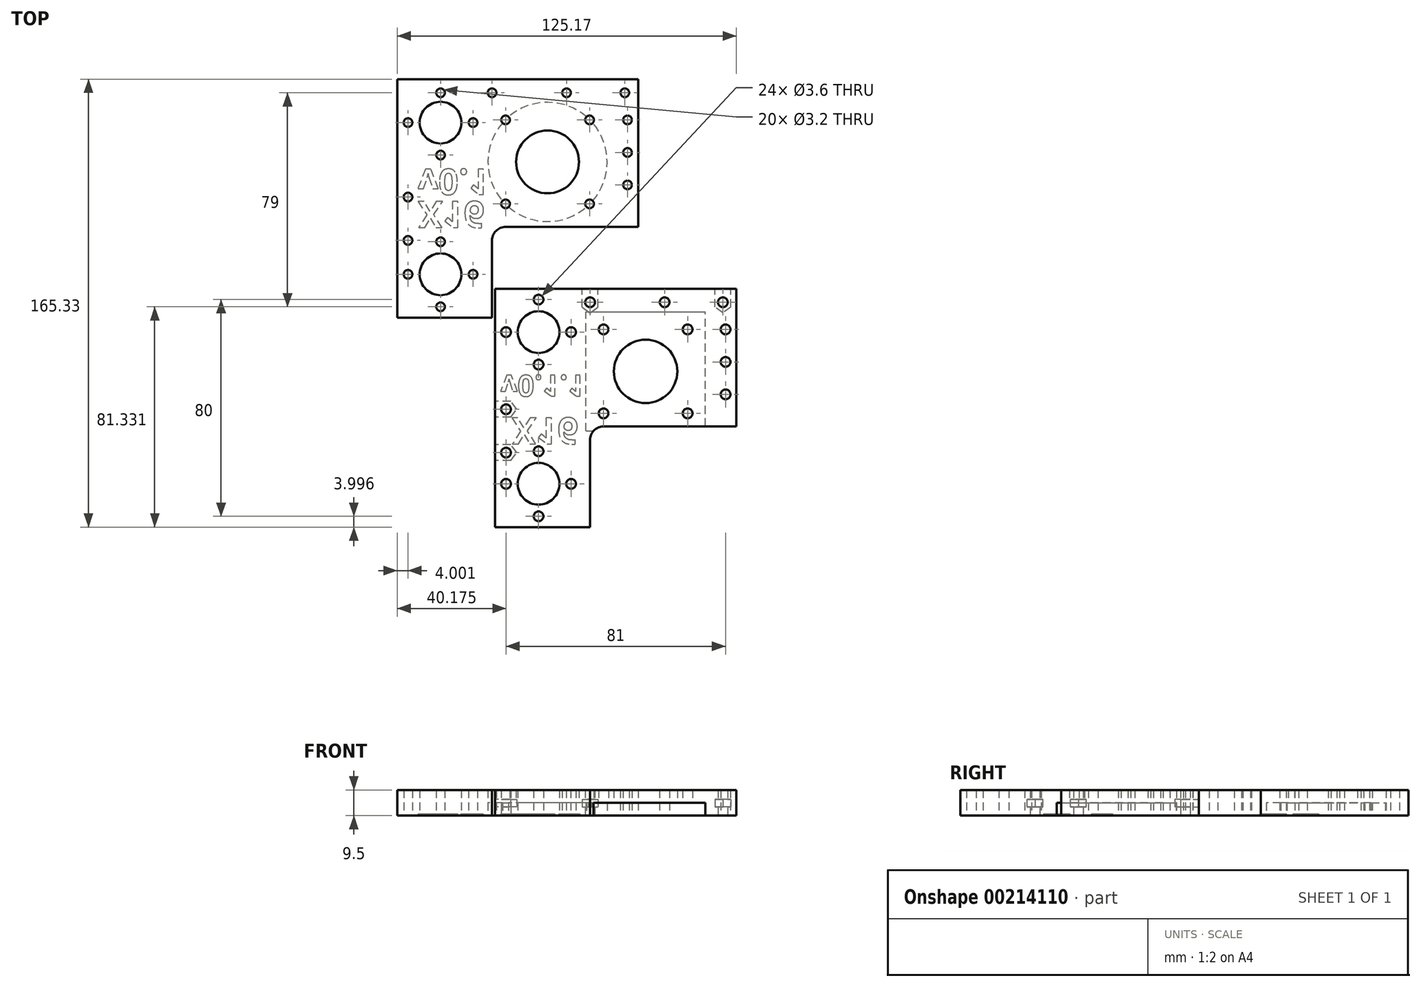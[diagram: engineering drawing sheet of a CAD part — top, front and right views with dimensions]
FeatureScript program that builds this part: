
annotation { "Feature Type Name" : "Feature", "Feature Type Description" : "" }
export const myFeature = defineFeature(function(context is Context, id is Id, definition is map)
    precondition{}
    {
        {
            var Q0;
            Q0=qCreatedBy(makeId("Top.planeOp"),FACE);
            var sketch = newSketch(context, id + "F0", { "sketchPlane" : qUnion([Q0])});
            skLineSegment(sketch, "E0", {"start": v(-66.99, 73.58) * mm, "end": v(-50.99, 73.58) * mm});
            skLineSegment(sketch, "E1", {"start": v(-50.99, 73.58) * mm, "end": v(-31.99, 73.58) * mm});
            skLineSegment(sketch, "E2", {"start": v(-31.99, 73.58) * mm, "end": v(-11.49, 73.58) * mm});
            skLineSegment(sketch, "E3", {"start": v(-11.49, 73.58) * mm, "end": v(-4.49, 73.58) * mm});
            skLineSegment(sketch, "E4", {"start": v(-4.49, 73.58) * mm, "end": v(22.01, 73.58) * mm});
            skLineSegment(sketch, "E5", {"start": v(22.01, 73.58) * mm, "end": v(22.01, 68.58) * mm});
            skLineSegment(sketch, "E6", {"start": v(22.01, 68.58) * mm, "end": v(22.01, 58.58) * mm});
            skLineSegment(sketch, "E7", {"start": v(22.01, 58.58) * mm, "end": v(22.01, 46.58) * mm});
            skLineSegment(sketch, "E8", {"start": v(22.01, 46.58) * mm, "end": v(22.01, 34.58) * mm});
            skLineSegment(sketch, "E9", {"start": v(22.01, 34.58) * mm, "end": v(22.01, 19.08) * mm});
            skPoint(sketch, "E10", {"position": v(22.01, 43.08) * mm});
            skPoint(sketch, "E11", {"position": v(17.01, 73.58) * mm});
            skLineSegment(sketch, "E12", {"start": v(-66.99, 73.58) * mm, "end": v(-66.99, 57.58) * mm});
            skLineSegment(sketch, "E13", {"start": v(-66.99, 57.58) * mm, "end": v(-66.99, 45.58) * mm});
            skLineSegment(sketch, "E14", {"start": v(-66.99, 45.58) * mm, "end": v(-66.99, 14.08) * mm});
            skPoint(sketch, "E15", {"position": v(-66.99, 30.08) * mm});
            skLineSegment(sketch, "E16", {"start": v(-66.99, 14.08) * mm, "end": v(-66.99, 1.58) * mm});
            skPoint(sketch, "E17", {"position": v(-66.99, 13.58) * mm});
            skLineSegment(sketch, "E18", {"start": v(-66.99, 1.58) * mm, "end": v(-66.99, -10.42) * mm});
            skLineSegment(sketch, "E19", {"start": v(-66.99, -10.42) * mm, "end": v(-66.99, -14.42) * mm});
            skLineSegment(sketch, "E20", {"start": v(-66.99, -14.42) * mm, "end": v(-50.99, -14.42) * mm});
            skLineSegment(sketch, "E21", {"start": v(-50.99, -14.42) * mm, "end": v(-31.99, -14.42) * mm});
            skLineSegment(sketch, "E22", {"start": v(-31.99, -14.42) * mm, "end": v(-31.99, 14.08) * mm});
            skLineSegment(sketch, "E23", {"start": v(-26.99, 19.08) * mm, "end": v(22.01, 19.08) * mm});
            skPoint(sketch, "E24.visualSharp", {"position": v(-31.99, 19.08) * mm});
            skArc(sketch, "E24.filletArc", {"start": v(-26.99, 19.08) * mm, "mid": v(-30.52, 17.62) * mm, "end": v(-31.99, 14.08) * mm});
            skPoint(sketch, "E25", {"position": v(-11.49, 19.08) * mm});
            skPoint(sketch, "E26", {"position": v(-26.99, 19.08) * mm});
            skPoint(sketch, "E27", {"position": v(4.01, 19.08) * mm});
            skPoint(sketch, "E28", {"position": v(-66.99, 69.58) * mm});
            skCircle(sketch, "E29", {"center": v(-11.49, 43.08) * mm, "radius": 11.6 * mm});
            skCircle(sketch, "E30", {"center": v(17.01, 68.58) * mm, "radius": 1.6 * mm});
            skCircle(sketch, "E31", {"center": v(-4.49, 68.58) * mm, "radius": 1.6 * mm});
            skCircle(sketch, "E32", {"center": v(-31.99, 68.58) * mm, "radius": 1.6 * mm});
            skCircle(sketch, "E33", {"center": v(-50.99, 68.58) * mm, "radius": 1.6 * mm});
            skCircle(sketch, "E34", {"center": v(-50.99, 57.58) * mm, "radius": 7.7 * mm});
            skCircle(sketch, "E35", {"center": v(-62.99, 57.58) * mm, "radius": 1.6 * mm});
            skCircle(sketch, "E36", {"center": v(-38.99, 57.58) * mm, "radius": 1.6 * mm});
            skCircle(sketch, "E37", {"center": v(-50.99, 45.58) * mm, "radius": 1.6 * mm});
            skCircle(sketch, "E38", {"center": v(-62.99, 30.08) * mm, "radius": 1.6 * mm});
            skCircle(sketch, "E39", {"center": v(-62.99, 14.08) * mm, "radius": 1.6 * mm});
            skCircle(sketch, "E40", {"center": v(-50.99, 1.58) * mm, "radius": 7.7 * mm});
            skCircle(sketch, "E41", {"center": v(-50.99, 13.58) * mm, "radius": 1.6 * mm});
            skCircle(sketch, "E42", {"center": v(-50.99, -10.42) * mm, "radius": 1.6 * mm});
            skCircle(sketch, "E43", {"center": v(-62.99, 1.58) * mm, "radius": 1.6 * mm});
            skCircle(sketch, "E44", {"center": v(-38.99, 1.58) * mm, "radius": 1.6 * mm});
            skCircle(sketch, "E45", {"center": v(18.01, 58.58) * mm, "radius": 1.6 * mm});
            skCircle(sketch, "E46", {"center": v(18.01, 46.58) * mm, "radius": 1.6 * mm});
            skCircle(sketch, "E47", {"center": v(18.01, 34.58) * mm, "radius": 1.6 * mm});
            skLineSegment(sketch, "E48", {"start": v(-11.49, 43.08) * mm, "end": v(-11.49, 58.58) * mm, "construction": true});
            skLineSegment(sketch, "E49", {"start": v(-11.49, 58.58) * mm, "end": v(-26.99, 58.58) * mm, "construction": true});
            skLineSegment(sketch, "E50", {"start": v(-26.99, 58.58) * mm, "end": v(-26.99, 27.58) * mm, "construction": true});
            skLineSegment(sketch, "E51", {"start": v(-26.99, 27.58) * mm, "end": v(4.01, 27.58) * mm, "construction": true});
            skLineSegment(sketch, "E52", {"start": v(4.01, 27.58) * mm, "end": v(4.01, 58.58) * mm, "construction": true});
            skCircle(sketch, "E53", {"center": v(-26.99, 58.58) * mm, "radius": 1.6 * mm});
            skCircle(sketch, "E54", {"center": v(4.01, 58.58) * mm, "radius": 1.6 * mm});
            skCircle(sketch, "E55", {"center": v(4.01, 27.58) * mm, "radius": 1.6 * mm});
            skCircle(sketch, "E56", {"center": v(-26.99, 27.58) * mm, "radius": 1.6 * mm});
            skSolve(sketch);
        }
        {
            var Q0;
            Q0 = qSketchRegion(id + "F0", true);
            extrude(context, id + "F1", {"entities" : qUnion([Q0]), "depth" : 9.5 * mm});
        }
        {
            var Q0;
            Q0=makeQuery(id+"F0.imprint","IMPRINT",FACE,{"disambiguationData":[TD([[makeQuery(id+"F0.imprint","IMPRINT",EDGE,{"derivedFrom":sQuery(id+"F0.wireOp",EDGE,"E0")}),-1.0]])]});
            var sketch = newSketch(context, id + "F2", { "sketchPlane" : qUnion([Q0])});
            skPoint(sketch, "E57.0", {"position": v(-11.49, 43.08) * mm});
            skCircle(sketch, "E58", {"center": v(-11.49, 43.08) * mm, "radius": 22 * mm});
            skSolve(sketch);
        }
        {
            var Q0;
            Q0 = qSketchRegion(id + "F2", true);
            extrude(context, id + "F3", {"entities" : qUnion([Q0]), "operationType" : NewBodyOperationType.REMOVE, "depth" : 4.8 * mm});
        }
        {
            var Q0;
            Q0=makeQuery(id+"F1.opExtrude","CAP_FACE",FACE,{"disambiguationData":[OSD([sQuery(id+"F0.wireOp",EDGE,"E0"),sQuery(id+"F0.wireOp",EDGE,"E1"),sQuery(id+"F0.wireOp",EDGE,"E2"),sQuery(id+"F0.wireOp",EDGE,"E3"),sQuery(id+"F0.wireOp",EDGE,"E4"),sQuery(id+"F0.wireOp",EDGE,"E5"),sQuery(id+"F0.wireOp",EDGE,"E6"),sQuery(id+"F0.wireOp",EDGE,"E7"),sQuery(id+"F0.wireOp",EDGE,"E8"),sQuery(id+"F0.wireOp",EDGE,"E9"),sQuery(id+"F0.wireOp",EDGE,"E12"),sQuery(id+"F0.wireOp",EDGE,"E13"),sQuery(id+"F0.wireOp",EDGE,"E14"),sQuery(id+"F0.wireOp",EDGE,"E16"),sQuery(id+"F0.wireOp",EDGE,"E18"),sQuery(id+"F0.wireOp",EDGE,"E19"),sQuery(id+"F0.wireOp",EDGE,"E20"),sQuery(id+"F0.wireOp",EDGE,"E21"),sQuery(id+"F0.wireOp",EDGE,"E22"),sQuery(id+"F0.wireOp",EDGE,"E23"),sQuery(id+"F0.wireOp",EDGE,"E24.filletArc"),sQuery(id+"F0.wireOp",EDGE,"E29"),sQuery(id+"F0.wireOp",EDGE,"E30"),sQuery(id+"F0.wireOp",EDGE,"E31"),sQuery(id+"F0.wireOp",EDGE,"E32"),sQuery(id+"F0.wireOp",EDGE,"E33"),sQuery(id+"F0.wireOp",EDGE,"E34"),sQuery(id+"F0.wireOp",EDGE,"E35"),sQuery(id+"F0.wireOp",EDGE,"E36"),sQuery(id+"F0.wireOp",EDGE,"E37"),sQuery(id+"F0.wireOp",EDGE,"E38"),sQuery(id+"F0.wireOp",EDGE,"E39"),sQuery(id+"F0.wireOp",EDGE,"E40"),sQuery(id+"F0.wireOp",EDGE,"E41"),sQuery(id+"F0.wireOp",EDGE,"E42"),sQuery(id+"F0.wireOp",EDGE,"E43"),sQuery(id+"F0.wireOp",EDGE,"E44"),sQuery(id+"F0.wireOp",EDGE,"E45"),sQuery(id+"F0.wireOp",EDGE,"E46"),sQuery(id+"F0.wireOp",EDGE,"E47"),sQuery(id+"F0.wireOp",EDGE,"E53"),sQuery(id+"F0.wireOp",EDGE,"E54"),sQuery(id+"F0.wireOp",EDGE,"E55"),sQuery(id+"F0.wireOp",EDGE,"E56")])],"isStart":true});
            var sketch = newSketch(context, id + "F4", { "sketchPlane" : qUnion([Q0])});
            skText(sketch, "E59", { "text": "X16", "fontName": "OpenSans-Bold.ttf"});
            skText(sketch, "E60", { "text": "v0.1", "fontName": "OpenSans-Bold.ttf"});
            const initialGuessF4  = {"E59": [-0.05927, -0.0285, 1, 0, 0.00977], "E60": [-0.05931, -0.0404, 1, 0, 0.00946]};
            skSetInitialGuess(sketch, initialGuessF4);
            skSolve(sketch);
        }
        {
            var Q0;
            Q0 = qSketchRegion(id + "F4", true);
            extrude(context, id + "F5", {"entities" : qUnion([Q0]), "operationType" : NewBodyOperationType.REMOVE, "oppositeDirection" : true, "depth" : .6 * mm});
        }
        {
            var Q0;
            Q0=qCreatedBy(makeId("Top.planeOp"),FACE);
            var sketch = newSketch(context, id + "F6", { "sketchPlane" : qUnion([Q0])});
            skLineSegment(sketch, "E61", {"start": v(-30.82, -3.75) * mm, "end": v(-14.82, -3.75) * mm});
            skLineSegment(sketch, "E62", {"start": v(-14.82, -3.75) * mm, "end": v(-14.82, -7.75) * mm, "construction": true});
            skLineSegment(sketch, "E63", {"start": v(-30.82, -3.75) * mm, "end": v(-30.82, -7.75) * mm});
            skLineSegment(sketch, "E64", {"start": v(-30.82, -7.75) * mm, "end": v(-30.82, -19.75) * mm});
            skLineSegment(sketch, "E65", {"start": v(-14.82, -7.75) * mm, "end": v(-14.82, -19.75) * mm, "construction": true});
            skCircle(sketch, "E66", {"center": v(-14.82, -19.75) * mm, "radius": 7.7 * mm});
            skCircle(sketch, "E67", {"center": v(-14.82, -7.75) * mm, "radius": 1.8 * mm});
            skLineSegment(sketch, "E68", {"start": v(-14.82, -19.75) * mm, "end": v(-26.82, -19.75) * mm, "construction": true});
            skLineSegment(sketch, "E69", {"start": v(-14.82, -19.75) * mm, "end": v(-2.82, -19.75) * mm, "construction": true});
            skLineSegment(sketch, "E70", {"start": v(-14.82, -19.75) * mm, "end": v(-14.82, -31.75) * mm, "construction": true});
            skCircle(sketch, "E71", {"center": v(-26.82, -19.75) * mm, "radius": 1.8 * mm});
            skCircle(sketch, "E72", {"center": v(-2.82, -19.75) * mm, "radius": 1.8 * mm});
            skCircle(sketch, "E73", {"center": v(-14.82, -31.75) * mm, "radius": 1.8 * mm});
            skLineSegment(sketch, "E74", {"start": v(-30.82, -19.75) * mm, "end": v(-30.82, -64.25) * mm});
            skLineSegment(sketch, "E75", {"start": v(-30.82, -64.25) * mm, "end": v(-26.82, -64.25) * mm, "construction": true});
            skLineSegment(sketch, "E76", {"start": v(-26.82, -64.25) * mm, "end": v(-26.82, -48.25) * mm, "construction": true});
            skCircle(sketch, "E77", {"center": v(-26.82, -64.25) * mm, "radius": 1.8 * mm});
            skCircle(sketch, "E78", {"center": v(-26.82, -48.25) * mm, "radius": 1.8 * mm});
            skLineSegment(sketch, "E79", {"start": v(-30.82, -64.25) * mm, "end": v(-30.82, -75.75) * mm});
            skLineSegment(sketch, "E80", {"start": v(-30.82, -75.75) * mm, "end": v(-14.82, -75.75) * mm, "construction": true});
            skCircle(sketch, "E81", {"center": v(-14.82, -75.75) * mm, "radius": 7.7 * mm});
            skLineSegment(sketch, "E82", {"start": v(-14.82, -75.75) * mm, "end": v(-14.82, -63.75) * mm, "construction": true});
            skLineSegment(sketch, "E83", {"start": v(-14.82, -75.75) * mm, "end": v(-2.82, -75.75) * mm, "construction": true});
            skLineSegment(sketch, "E84", {"start": v(-14.82, -75.75) * mm, "end": v(-14.82, -87.75) * mm, "construction": true});
            skLineSegment(sketch, "E85", {"start": v(-14.82, -75.75) * mm, "end": v(-26.82, -75.75) * mm, "construction": true});
            skCircle(sketch, "E86", {"center": v(-14.82, -63.75) * mm, "radius": 1.8 * mm});
            skCircle(sketch, "E87", {"center": v(-2.82, -75.75) * mm, "radius": 1.8 * mm});
            skCircle(sketch, "E88", {"center": v(-14.82, -87.75) * mm, "radius": 1.8 * mm});
            skCircle(sketch, "E89", {"center": v(-26.82, -75.75) * mm, "radius": 1.8 * mm});
            skLineSegment(sketch, "E90", {"start": v(-30.82, -75.75) * mm, "end": v(-30.82, -91.75) * mm});
            skLineSegment(sketch, "E91", {"start": v(-30.82, -91.75) * mm, "end": v(4.18, -91.75) * mm});
            skLineSegment(sketch, "E92", {"start": v(-14.82, -3.75) * mm, "end": v(4.18, -3.75) * mm});
            skLineSegment(sketch, "E93", {"start": v(4.18, -3.75) * mm, "end": v(4.18, -8.75) * mm, "construction": true});
            skCircle(sketch, "E94", {"center": v(4.18, -8.75) * mm, "radius": 1.8 * mm});
            skLineSegment(sketch, "E95", {"start": v(4.18, -3.75) * mm, "end": v(24.68, -3.75) * mm});
            skLineSegment(sketch, "E96", {"start": v(24.68, -3.75) * mm, "end": v(24.68, -34.25) * mm, "construction": true});
            skLineSegment(sketch, "E97", {"start": v(24.68, -3.75) * mm, "end": v(31.68, -3.75) * mm});
            skLineSegment(sketch, "E98", {"start": v(31.68, -3.75) * mm, "end": v(31.68, -8.75) * mm, "construction": true});
            skCircle(sketch, "E99", {"center": v(31.68, -8.75) * mm, "radius": 1.8 * mm});
            skLineSegment(sketch, "E100", {"start": v(31.68, -3.75) * mm, "end": v(58.18, -3.75) * mm});
            skLineSegment(sketch, "E101", {"start": v(58.18, -3.75) * mm, "end": v(53.18, -3.75) * mm, "construction": true});
            skLineSegment(sketch, "E102", {"start": v(53.18, -3.75) * mm, "end": v(53.18, -8.75) * mm, "construction": true});
            skCircle(sketch, "E103", {"center": v(53.18, -8.75) * mm, "radius": 1.8 * mm});
            skLineSegment(sketch, "E104", {"start": v(58.18, -3.75) * mm, "end": v(58.18, -54.55) * mm});
            skLineSegment(sketch, "E105", {"start": v(58.18, -54.55) * mm, "end": v(9.18, -54.55) * mm});
            skLineSegment(sketch, "E106", {"start": v(4.18, -59.55) * mm, "end": v(4.18, -91.75) * mm});
            skPoint(sketch, "E107.visualSharp", {"position": v(4.18, -54.55) * mm});
            skArc(sketch, "E107.filletArc", {"start": v(9.18, -54.55) * mm, "mid": v(5.65, -56.02) * mm, "end": v(4.18, -59.55) * mm});
            skLineSegment(sketch, "E108", {"start": v(58.18, -3.75) * mm, "end": v(58.18, -18.75) * mm, "construction": true});
            skLineSegment(sketch, "E109", {"start": v(58.18, -18.75) * mm, "end": v(58.18, -30.75) * mm, "construction": true});
            skLineSegment(sketch, "E110", {"start": v(58.18, -30.75) * mm, "end": v(58.18, -42.75) * mm, "construction": true});
            skLineSegment(sketch, "E111", {"start": v(58.18, -42.75) * mm, "end": v(54.18, -42.75) * mm, "construction": true});
            skLineSegment(sketch, "E112", {"start": v(58.18, -30.75) * mm, "end": v(54.18, -30.75) * mm, "construction": true});
            skLineSegment(sketch, "E113", {"start": v(58.18, -18.75) * mm, "end": v(54.18, -18.75) * mm, "construction": true});
            skCircle(sketch, "E114", {"center": v(54.18, -18.75) * mm, "radius": 1.8 * mm});
            skCircle(sketch, "E115", {"center": v(54.18, -30.75) * mm, "radius": 1.8 * mm});
            skCircle(sketch, "E116", {"center": v(54.18, -42.75) * mm, "radius": 1.8 * mm});
            skCircle(sketch, "E117", {"center": v(24.68, -34.25) * mm, "radius": 11.7 * mm});
            skLineSegment(sketch, "E118", {"start": v(24.68, -34.25) * mm, "end": v(24.68, -18.75) * mm, "construction": true});
            skLineSegment(sketch, "E119", {"start": v(24.68, -18.75) * mm, "end": v(9.18, -18.75) * mm, "construction": true});
            skLineSegment(sketch, "E120", {"start": v(9.18, -18.75) * mm, "end": v(9.18, -49.75) * mm, "construction": true});
            skLineSegment(sketch, "E121", {"start": v(9.18, -49.75) * mm, "end": v(40.18, -49.75) * mm, "construction": true});
            skLineSegment(sketch, "E122", {"start": v(40.18, -49.75) * mm, "end": v(40.18, -18.75) * mm, "construction": true});
            skCircle(sketch, "E123", {"center": v(9.18, -18.75) * mm, "radius": 1.8 * mm});
            skCircle(sketch, "E124", {"center": v(40.18, -18.75) * mm, "radius": 1.8 * mm});
            skCircle(sketch, "E125", {"center": v(40.18, -49.75) * mm, "radius": 1.8 * mm});
            skCircle(sketch, "E126", {"center": v(9.18, -49.75) * mm, "radius": 1.8 * mm});
            skSolve(sketch);
        }
        {
            var Q0;
            Q0 = qSketchRegion(id + "F6", true);
            extrude(context, id + "F7", {"entities" : qUnion([Q0]), "depth" : 9.5 * mm});
        }
        {
            var Q0;
            Q0=makeQuery(id+"F7.opExtrude","CAP_FACE",FACE,{"disambiguationData":[OSD([sQuery(id+"F6.wireOp",EDGE,"E61"),sQuery(id+"F6.wireOp",EDGE,"E63"),sQuery(id+"F6.wireOp",EDGE,"E64"),sQuery(id+"F6.wireOp",EDGE,"E66"),sQuery(id+"F6.wireOp",EDGE,"E67"),sQuery(id+"F6.wireOp",EDGE,"E71"),sQuery(id+"F6.wireOp",EDGE,"E72"),sQuery(id+"F6.wireOp",EDGE,"E73"),sQuery(id+"F6.wireOp",EDGE,"E74"),sQuery(id+"F6.wireOp",EDGE,"E77"),sQuery(id+"F6.wireOp",EDGE,"E78"),sQuery(id+"F6.wireOp",EDGE,"E79"),sQuery(id+"F6.wireOp",EDGE,"E81"),sQuery(id+"F6.wireOp",EDGE,"E86"),sQuery(id+"F6.wireOp",EDGE,"E87"),sQuery(id+"F6.wireOp",EDGE,"E88"),sQuery(id+"F6.wireOp",EDGE,"E89"),sQuery(id+"F6.wireOp",EDGE,"E90"),sQuery(id+"F6.wireOp",EDGE,"E91"),sQuery(id+"F6.wireOp",EDGE,"E92"),sQuery(id+"F6.wireOp",EDGE,"E94"),sQuery(id+"F6.wireOp",EDGE,"E95"),sQuery(id+"F6.wireOp",EDGE,"E97"),sQuery(id+"F6.wireOp",EDGE,"E99"),sQuery(id+"F6.wireOp",EDGE,"E100"),sQuery(id+"F6.wireOp",EDGE,"E103"),sQuery(id+"F6.wireOp",EDGE,"E104"),sQuery(id+"F6.wireOp",EDGE,"E105"),sQuery(id+"F6.wireOp",EDGE,"E106"),sQuery(id+"F6.wireOp",EDGE,"E107.filletArc"),sQuery(id+"F6.wireOp",EDGE,"E114"),sQuery(id+"F6.wireOp",EDGE,"E115"),sQuery(id+"F6.wireOp",EDGE,"E116"),sQuery(id+"F6.wireOp",EDGE,"E117"),sQuery(id+"F6.wireOp",EDGE,"E123"),sQuery(id+"F6.wireOp",EDGE,"E124"),sQuery(id+"F6.wireOp",EDGE,"E125"),sQuery(id+"F6.wireOp",EDGE,"E126")])],"isStart":true});
            var sketch = newSketch(context, id + "F8", { "sketchPlane" : qUnion([Q0])});
            skCircle(sketch, "E127.0", {"center": v(24.68, 34.25) * mm, "radius": 11.7 * mm, "construction": true});
            skLineSegment(sketch, "E128.bottom", {"start": v(2.68, 56.25) * mm, "end": v(46.68, 56.25) * mm});
            skLineSegment(sketch, "E128.top", {"start": v(2.68, 12.25) * mm, "end": v(46.68, 12.25) * mm});
            skLineSegment(sketch, "E128.left", {"start": v(2.68, 56.25) * mm, "end": v(2.68, 12.25) * mm});
            skLineSegment(sketch, "E128.right", {"start": v(46.68, 56.25) * mm, "end": v(46.68, 12.25) * mm});
            skPoint(sketch, "E129", {"position": v(24.68, 12.25) * mm});
            skPoint(sketch, "E130", {"position": v(46.68, 34.25) * mm});
            skSolve(sketch);
        }
        {
            var Q0;
            Q0 = qSketchRegion(id + "F8", true);
            extrude(context, id + "F9", {"entities" : qUnion([Q0]), "operationType" : NewBodyOperationType.REMOVE, "oppositeDirection" : true, "depth" : 4.8 * mm});
        }
        {
            var Q0;
            Q0=makeQuery(id+"F7.opExtrude","CAP_FACE",FACE,{"disambiguationData":[OSD([sQuery(id+"F6.wireOp",EDGE,"E61"),sQuery(id+"F6.wireOp",EDGE,"E63"),sQuery(id+"F6.wireOp",EDGE,"E64"),sQuery(id+"F6.wireOp",EDGE,"E66"),sQuery(id+"F6.wireOp",EDGE,"E67"),sQuery(id+"F6.wireOp",EDGE,"E71"),sQuery(id+"F6.wireOp",EDGE,"E72"),sQuery(id+"F6.wireOp",EDGE,"E73"),sQuery(id+"F6.wireOp",EDGE,"E74"),sQuery(id+"F6.wireOp",EDGE,"E77"),sQuery(id+"F6.wireOp",EDGE,"E78"),sQuery(id+"F6.wireOp",EDGE,"E79"),sQuery(id+"F6.wireOp",EDGE,"E81"),sQuery(id+"F6.wireOp",EDGE,"E86"),sQuery(id+"F6.wireOp",EDGE,"E87"),sQuery(id+"F6.wireOp",EDGE,"E88"),sQuery(id+"F6.wireOp",EDGE,"E89"),sQuery(id+"F6.wireOp",EDGE,"E90"),sQuery(id+"F6.wireOp",EDGE,"E91"),sQuery(id+"F6.wireOp",EDGE,"E92"),sQuery(id+"F6.wireOp",EDGE,"E94"),sQuery(id+"F6.wireOp",EDGE,"E95"),sQuery(id+"F6.wireOp",EDGE,"E97"),sQuery(id+"F6.wireOp",EDGE,"E99"),sQuery(id+"F6.wireOp",EDGE,"E100"),sQuery(id+"F6.wireOp",EDGE,"E103"),sQuery(id+"F6.wireOp",EDGE,"E104"),sQuery(id+"F6.wireOp",EDGE,"E105"),sQuery(id+"F6.wireOp",EDGE,"E106"),sQuery(id+"F6.wireOp",EDGE,"E107.filletArc"),sQuery(id+"F6.wireOp",EDGE,"E114"),sQuery(id+"F6.wireOp",EDGE,"E115"),sQuery(id+"F6.wireOp",EDGE,"E116"),sQuery(id+"F6.wireOp",EDGE,"E117"),sQuery(id+"F6.wireOp",EDGE,"E123"),sQuery(id+"F6.wireOp",EDGE,"E124"),sQuery(id+"F6.wireOp",EDGE,"E125"),sQuery(id+"F6.wireOp",EDGE,"E126")])],"isStart":true});
            var sketch = newSketch(context, id + "F10", { "sketchPlane" : qUnion([Q0])});
            skText(sketch, "E131", { "text": "X16", "fontName": "OpenSans-Bold.ttf"});
            skText(sketch, "E132", { "text": "v0.1.1", "fontName": "OpenSans-Bold.ttf"});
            const initialGuessF10  = {"E131": [-0.02468, 0.05138, 1, 0, 0.00977], "E132": [-0.02879, 0.03567, 1, 0, 0.00783]};
            skSetInitialGuess(sketch, initialGuessF10);
            skSolve(sketch);
        }
        {
            var Q0;
            Q0=makeQuery(id+"F10.imprint","IMPRINT",FACE,{"disambiguationData":[TD([[makeQuery(id+"F10.imprint","IMPRINT",EDGE,{"derivedFrom":sQuery(id+"F10.wireOp",EDGE,"E132.sketch_text.stroke-10")}),-1.0]])]});
            var Q1;
            Q1=makeQuery(id+"F10.imprint","IMPRINT",FACE,{"disambiguationData":[TD([[makeQuery(id+"F10.imprint","IMPRINT",EDGE,{"derivedFrom":sQuery(id+"F10.wireOp",EDGE,"E132.sketch_text.stroke-0")}),-1.0]])]});
            var Q2;
            Q2=makeQuery(id+"F10.imprint","IMPRINT",FACE,{"disambiguationData":[TD([[makeQuery(id+"F10.imprint","IMPRINT",EDGE,{"derivedFrom":sQuery(id+"F10.wireOp",EDGE,"E132.sketch_text.stroke-26")}),-1.0]])]});
            var Q3;
            Q3=makeQuery(id+"F10.imprint","IMPRINT",FACE,{"disambiguationData":[TD([[makeQuery(id+"F10.imprint","IMPRINT",EDGE,{"derivedFrom":sQuery(id+"F10.wireOp",EDGE,"E132.sketch_text.stroke-34")}),-1.0]])]});
            var Q4;
            Q4=makeQuery(id+"F10.imprint","IMPRINT",FACE,{"disambiguationData":[TD([[makeQuery(id+"F10.imprint","IMPRINT",EDGE,{"derivedFrom":sQuery(id+"F10.wireOp",EDGE,"E132.sketch_text.stroke-44")}),-1.0]])]});
            var Q5;
            Q5=makeQuery(id+"F10.imprint","IMPRINT",FACE,{"disambiguationData":[TD([[makeQuery(id+"F10.imprint","IMPRINT",EDGE,{"derivedFrom":sQuery(id+"F10.wireOp",EDGE,"E132.sketch_text.stroke-52")}),-1.0]])]});
            var Q6;
            Q6=makeQuery(id+"F10.imprint","IMPRINT",FACE,{"disambiguationData":[TD([[makeQuery(id+"F10.imprint","IMPRINT",EDGE,{"derivedFrom":sQuery(id+"F10.wireOp",EDGE,"E131.sketch_text.stroke-22")}),-1.0]])]});
            var Q7;
            Q7=makeQuery(id+"F10.imprint","IMPRINT",FACE,{"disambiguationData":[TD([[makeQuery(id+"F10.imprint","IMPRINT",EDGE,{"derivedFrom":sQuery(id+"F10.wireOp",EDGE,"E131.sketch_text.stroke-12")}),-1.0]])]});
            var Q8;
            Q8=makeQuery(id+"F10.imprint","IMPRINT",FACE,{"disambiguationData":[TD([[makeQuery(id+"F10.imprint","IMPRINT",EDGE,{"derivedFrom":sQuery(id+"F10.wireOp",EDGE,"E131.sketch_text.stroke-0")}),-1.0]])]});
            extrude(context, id + "F11", {"entities" : qUnion([Q0, Q1, Q2, Q3, Q4, Q5, Q6, Q7, Q8]), "operationType" : NewBodyOperationType.REMOVE, "oppositeDirection" : true, "depth" : .6 * mm});
        }
        {
            var Q0;
            Q0=makeQuery(id+"F7.opExtrude","SWEPT_FACE",FACE,{"disambiguationData":[OSD([sQuery(id+"F6.wireOp",EDGE,"E63"),sQuery(id+"F6.wireOp",EDGE,"E64"),sQuery(id+"F6.wireOp",EDGE,"E74"),sQuery(id+"F6.wireOp",EDGE,"E79"),sQuery(id+"F6.wireOp",EDGE,"E90")])]});
            var sketch = newSketch(context, id + "F12", { "sketchPlane" : qUnion([Q0])});
            skLineSegment(sketch, "E133", {"start": v(3.75, 0) * mm, "end": v(64.25, 0) * mm, "construction": true});
            skLineSegment(sketch, "E134", {"start": v(64.25, 0) * mm, "end": v(64.25, 3.2) * mm, "construction": true});
            skLineSegment(sketch, "E135", {"start": v(64.25, 3.2) * mm, "end": v(64.25, 6) * mm, "construction": true});
            skLineSegment(sketch, "E136.bottom", {"start": v(61.35, 3.2) * mm, "end": v(67.15, 3.2) * mm});
            skLineSegment(sketch, "E136.top", {"start": v(61.35, 6) * mm, "end": v(67.15, 6) * mm});
            skLineSegment(sketch, "E136.left", {"start": v(61.35, 3.2) * mm, "end": v(61.35, 6) * mm});
            skLineSegment(sketch, "E136.right", {"start": v(67.15, 3.2) * mm, "end": v(67.15, 6) * mm});
            skLineSegment(sketch, "E137", {"start": v(64.25, 0) * mm, "end": v(48.25, 0) * mm, "construction": true});
            skLineSegment(sketch, "E138", {"start": v(48.25, 0) * mm, "end": v(48.25, 3.2) * mm, "construction": true});
            skLineSegment(sketch, "E139", {"start": v(48.25, 3.2) * mm, "end": v(48.25, 6) * mm, "construction": true});
            skLineSegment(sketch, "E140.bottom", {"start": v(45.35, 3.2) * mm, "end": v(51.15, 3.2) * mm});
            skLineSegment(sketch, "E140.top", {"start": v(45.35, 6) * mm, "end": v(51.15, 6) * mm});
            skLineSegment(sketch, "E140.left", {"start": v(45.35, 3.2) * mm, "end": v(45.35, 6) * mm});
            skLineSegment(sketch, "E140.right", {"start": v(51.15, 3.2) * mm, "end": v(51.15, 6) * mm});
            skSolve(sketch);
        }
        {
            var Q0;
            Q0 = qSketchRegion(id + "F12", true);
            extrude(context, id + "F13", {"entities" : qUnion([Q0]), "operationType" : NewBodyOperationType.REMOVE, "oppositeDirection" : true, "depth" : 5.8 * mm});
        }
        {
            var Q0;
            Q0=makeQuery(id+"F7.opExtrude","SWEPT_FACE",FACE,{"disambiguationData":[OSD([sQuery(id+"F6.wireOp",EDGE,"E61"),sQuery(id+"F6.wireOp",EDGE,"E92"),sQuery(id+"F6.wireOp",EDGE,"E95"),sQuery(id+"F6.wireOp",EDGE,"E97"),sQuery(id+"F6.wireOp",EDGE,"E100")])]});
            var sketch = newSketch(context, id + "F14", { "sketchPlane" : qUnion([Q0])});
            skLineSegment(sketch, "E141", {"start": v(30.82, 0) * mm, "end": v(-4.18, 0) * mm, "construction": true});
            skLineSegment(sketch, "E142", {"start": v(-4.18, 0) * mm, "end": v(-4.18, 3.2) * mm, "construction": true});
            skLineSegment(sketch, "E143", {"start": v(-4.18, 3.2) * mm, "end": v(-4.18, 6) * mm, "construction": true});
            skLineSegment(sketch, "E144", {"start": v(-58.18, 0) * mm, "end": v(-53.18, 0) * mm, "construction": true});
            skLineSegment(sketch, "E145", {"start": v(-53.18, 0) * mm, "end": v(-53.18, 3.2) * mm, "construction": true});
            skLineSegment(sketch, "E146", {"start": v(-53.18, 3.2) * mm, "end": v(-53.18, 6) * mm, "construction": true});
            skLineSegment(sketch, "E147.bottom", {"start": v(-1.28, 6) * mm, "end": v(-7.08, 6) * mm});
            skLineSegment(sketch, "E147.top", {"start": v(-1.28, 3.2) * mm, "end": v(-7.08, 3.2) * mm});
            skLineSegment(sketch, "E147.left", {"start": v(-1.28, 6) * mm, "end": v(-1.28, 3.2) * mm});
            skLineSegment(sketch, "E147.right", {"start": v(-7.08, 6) * mm, "end": v(-7.08, 3.2) * mm});
            skLineSegment(sketch, "E148.bottom", {"start": v(-50.28, 6) * mm, "end": v(-56.08, 6) * mm});
            skLineSegment(sketch, "E148.top", {"start": v(-50.28, 3.2) * mm, "end": v(-56.08, 3.2) * mm});
            skLineSegment(sketch, "E148.left", {"start": v(-50.28, 6) * mm, "end": v(-50.28, 3.2) * mm});
            skLineSegment(sketch, "E148.right", {"start": v(-56.08, 6) * mm, "end": v(-56.08, 3.2) * mm});
            skSolve(sketch);
        }
        {
            var Q0;
            Q0 = qSketchRegion(id + "F14", true);
            extrude(context, id + "F15", {"entities" : qUnion([Q0]), "operationType" : NewBodyOperationType.REMOVE, "oppositeDirection" : true, "depth" : 6.8 * mm});
        }
        {
            var Q0;
            Q0=makeQuery(id+"F15.boolean.opBoolean","COPY",FACE,{"derivedFrom":makeQuery(id+"F15.opExtrude","SWEPT_FACE",FACE,{"disambiguationData":[OSD([sQuery(id+"F14.wireOp",EDGE,"E147.top")])]})});
            var sketch = newSketch(context, id + "F16", { "sketchPlane" : qUnion([Q0])});
            skLineSegment(sketch, "E149", {"start": v(1.28, -10.55) * mm, "end": v(4.18, -12.69) * mm});
            skLineSegment(sketch, "E150", {"start": v(4.18, -12.69) * mm, "end": v(7.08, -10.55) * mm});
            skLineSegment(sketch, "E151", {"start": v(7.08, -10.55) * mm, "end": v(1.28, -10.55) * mm});
            skPoint(sketch, "E152.0", {"position": v(50.28, -10.55) * mm});
            skPoint(sketch, "E153.0", {"position": v(56.08, -10.55) * mm});
            skLineSegment(sketch, "E154", {"start": v(50.28, -10.55) * mm, "end": v(56.08, -10.55) * mm});
            skLineSegment(sketch, "E155", {"start": v(56.08, -10.55) * mm, "end": v(53.18, -12.69) * mm});
            skLineSegment(sketch, "E156", {"start": v(53.18, -12.69) * mm, "end": v(50.28, -10.55) * mm});
            skPoint(sketch, "E157.0", {"position": v(-25.02, -45.35) * mm});
            skPoint(sketch, "E158.0", {"position": v(-25.02, -51.15) * mm});
            skPoint(sketch, "E159.0", {"position": v(-25.02, -67.15) * mm});
            skPoint(sketch, "E160.0", {"position": v(-25.02, -61.35) * mm});
            skLineSegment(sketch, "E161", {"start": v(-25.02, -61.35) * mm, "end": v(-25.02, -67.15) * mm});
            skLineSegment(sketch, "E162", {"start": v(-25.02, -67.15) * mm, "end": v(-22.88, -64.25) * mm});
            skLineSegment(sketch, "E163", {"start": v(-22.88, -64.25) * mm, "end": v(-25.02, -61.35) * mm});
            skLineSegment(sketch, "E164", {"start": v(-25.02, -51.15) * mm, "end": v(-22.88, -48.25) * mm});
            skLineSegment(sketch, "E165", {"start": v(-22.88, -48.25) * mm, "end": v(-25.02, -45.35) * mm});
            skLineSegment(sketch, "E166", {"start": v(-25.02, -45.35) * mm, "end": v(-25.02, -51.15) * mm});
            skSolve(sketch);
        }
        {
            var Q0;
            Q0 = qSketchRegion(id + "F16", true);
            extrude(context, id + "F17", {"entities" : qUnion([Q0]), "operationType" : NewBodyOperationType.REMOVE, "depth" : 2.8 * mm});
        }
    });
